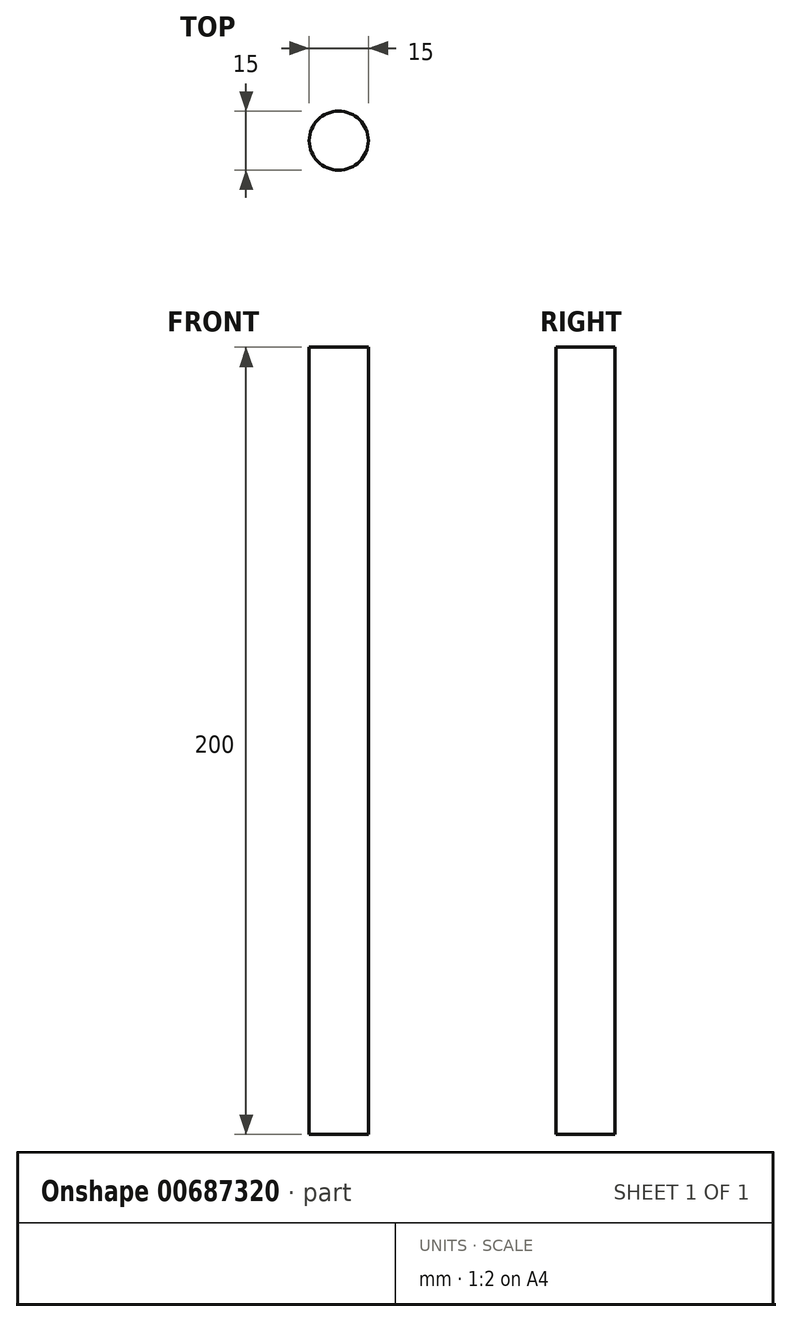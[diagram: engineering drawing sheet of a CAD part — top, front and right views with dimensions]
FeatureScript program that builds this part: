
annotation { "Feature Type Name" : "Feature", "Feature Type Description" : "" }
export const myFeature = defineFeature(function(context is Context, id is Id, definition is map)
    precondition{}
    {
        {
            var Q0;
            Q0=qCreatedBy(makeId("Top.planeOp"),FACE);
            var sketch = newSketch(context, id + "F0", { "sketchPlane" : qUnion([Q0])});
            skCircle(sketch, "E0", {"center": v(0, 0) * mm, "radius": 7.5 * mm});
            skSolve(sketch);
        }
        {
            var Q0;
            Q0=makeQuery(id+"F0.imprint","IMPRINT",FACE,{"disambiguationData":[TD([[makeQuery(id+"F0.imprint","IMPRINT",EDGE,{"derivedFrom":sQuery(id+"F0.wireOp",EDGE,"E0")}),1.0]])]});
            extrude(context, id + "F1", {"entities" : qUnion([Q0]), "endBound" : BoundingType.SYMMETRIC, "depth" : 200 * mm, "offsetDistance" : 25 * mm});
        }
    });
